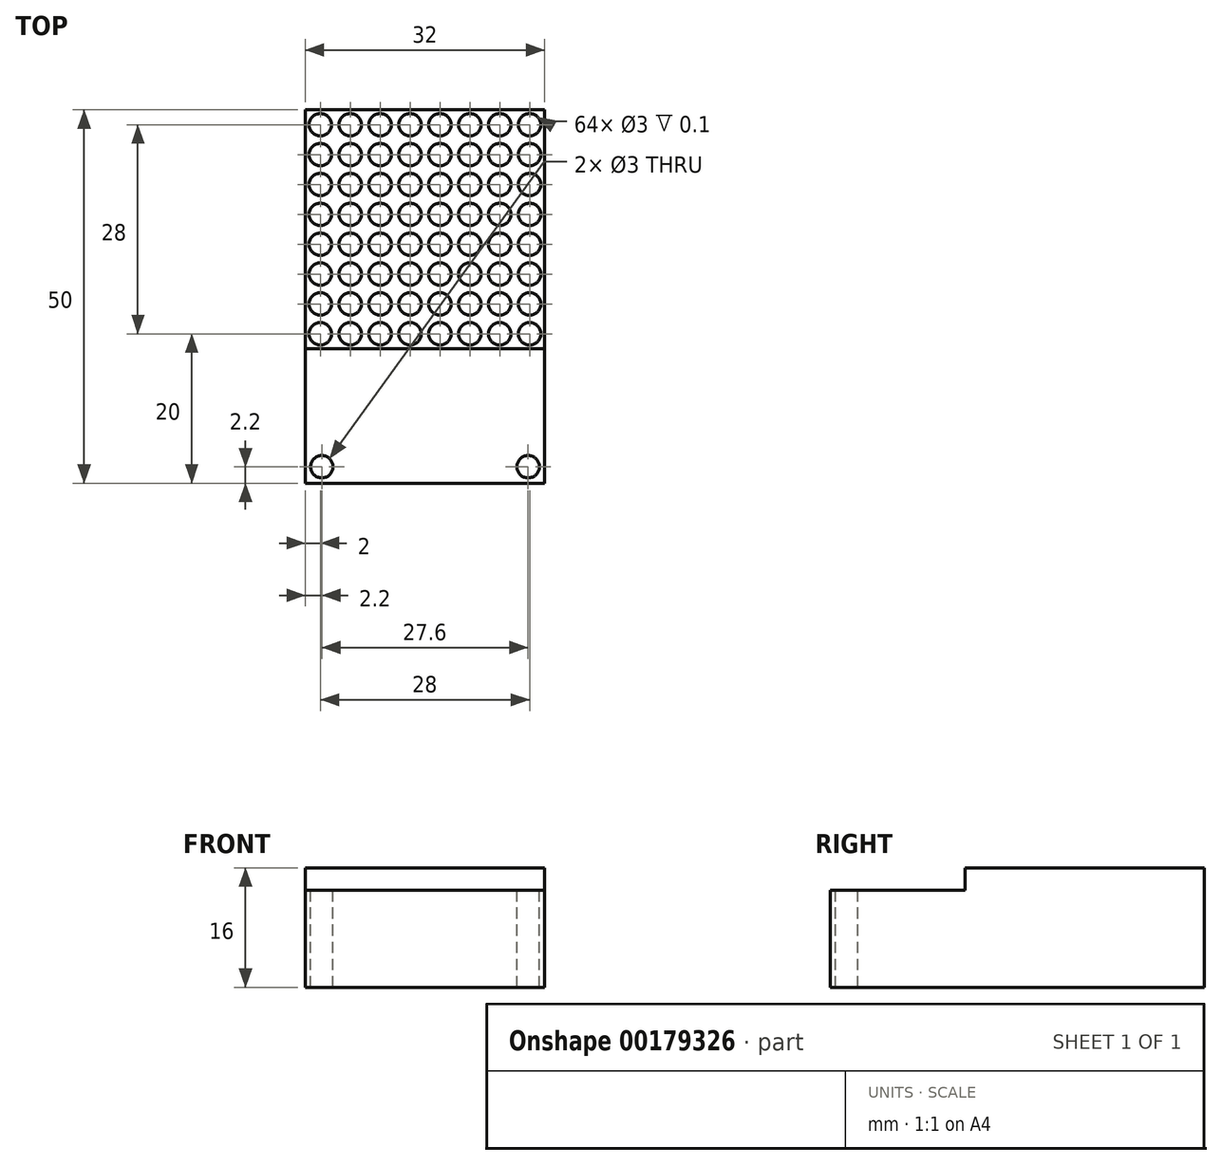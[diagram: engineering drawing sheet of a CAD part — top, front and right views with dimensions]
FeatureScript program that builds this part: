
annotation { "Feature Type Name" : "Feature", "Feature Type Description" : "" }
export const myFeature = defineFeature(function(context is Context, id is Id, definition is map)
    precondition{}
    {
        {
            var Q0;
            Q0=qCreatedBy(makeId("Top.planeOp"),FACE);
            var sketch = newSketch(context, id + "F0", { "sketchPlane" : qUnion([Q0])});
            skLineSegment(sketch, "E0.bottom", {"start": v(16, 16) * mm, "end": v(-16, 16) * mm});
            skLineSegment(sketch, "E0.top", {"start": v(16, -16) * mm, "end": v(-16, -16) * mm});
            skLineSegment(sketch, "E0.left", {"start": v(16, 16) * mm, "end": v(16, -16) * mm});
            skLineSegment(sketch, "E0.right", {"start": v(-16, 16) * mm, "end": v(-16, -16) * mm});
            skPoint(sketch, "E0.middle", {"position": v(0, 0) * mm});
            skSolve(sketch);
        }
        {
            var Q0;
            Q0=makeQuery(id+"F0.imprint","IMPRINT",FACE,{"disambiguationData":[TD([[makeQuery(id+"F0.imprint","IMPRINT",EDGE,{"derivedFrom":sQuery(id+"F0.wireOp",EDGE,"E0.bottom")}),1.0]])]});
            extrude(context, id + "F1", {"entities" : qUnion([Q0]), "depth" : 3 * mm});
        }
        {
            var Q0;
            Q0=makeQuery(id+"F1.opExtrude","CAP_FACE",FACE,{"disambiguationData":[OSD([sQuery(id+"F0.wireOp",EDGE,"E0.bottom"),sQuery(id+"F0.wireOp",EDGE,"E0.top"),sQuery(id+"F0.wireOp",EDGE,"E0.left"),sQuery(id+"F0.wireOp",EDGE,"E0.right")])],"isStart":true});
            var sketch = newSketch(context, id + "F2", { "sketchPlane" : qUnion([Q0])});
            skLineSegment(sketch, "E1.bottom", {"start": v(16, -16) * mm, "end": v(-16, -16) * mm});
            skLineSegment(sketch, "E1.top", {"start": v(16, 34) * mm, "end": v(-16, 34) * mm});
            skLineSegment(sketch, "E1.left", {"start": v(16, -16) * mm, "end": v(16, 34) * mm});
            skLineSegment(sketch, "E1.right", {"start": v(-16, -16) * mm, "end": v(-16, 34) * mm});
            skSolve(sketch);
        }
        {
            var Q0;
            Q0 = qSketchRegion(id + "F2", true);
            extrude(context, id + "F3", {"entities" : qUnion([Q0]), "operationType" : NewBodyOperationType.ADD, "depth" : 13 * mm});
        }
        {
            var Q0;
            Q0=makeQuery(id+"F1.opExtrude","CAP_FACE",FACE,{"disambiguationData":[OSD([sQuery(id+"F0.wireOp",EDGE,"E0.bottom"),sQuery(id+"F0.wireOp",EDGE,"E0.top"),sQuery(id+"F0.wireOp",EDGE,"E0.left"),sQuery(id+"F0.wireOp",EDGE,"E0.right")])],"isStart":false});
            var sketch = newSketch(context, id + "F4", { "sketchPlane" : qUnion([Q0])});
            skCircle(sketch, "E2", {"center": v(14, 14) * mm, "radius": 1.5 * mm});
            skCircle(sketch, "E3.0.1.0", {"center": v(14, 10) * mm, "radius": 1.5 * mm});
            skCircle(sketch, "E3.0.2.0", {"center": v(14, 6) * mm, "radius": 1.5 * mm});
            skCircle(sketch, "E3.0.3.0", {"center": v(14, 2) * mm, "radius": 1.5 * mm});
            skCircle(sketch, "E3.0.4.0", {"center": v(14, -2) * mm, "radius": 1.5 * mm});
            skCircle(sketch, "E3.0.5.0", {"center": v(14, -6) * mm, "radius": 1.5 * mm});
            skCircle(sketch, "E3.0.6.0", {"center": v(14, -10) * mm, "radius": 1.5 * mm});
            skCircle(sketch, "E3.0.7.0", {"center": v(14, -14) * mm, "radius": 1.5 * mm});
            skCircle(sketch, "E3.1.0.0", {"center": v(10, 14) * mm, "radius": 1.5 * mm});
            skCircle(sketch, "E3.1.1.0", {"center": v(10, 10) * mm, "radius": 1.5 * mm});
            skCircle(sketch, "E3.1.2.0", {"center": v(10, 6) * mm, "radius": 1.5 * mm});
            skCircle(sketch, "E3.1.3.0", {"center": v(10, 2) * mm, "radius": 1.5 * mm});
            skCircle(sketch, "E3.1.4.0", {"center": v(10, -2) * mm, "radius": 1.5 * mm});
            skCircle(sketch, "E3.1.5.0", {"center": v(10, -6) * mm, "radius": 1.5 * mm});
            skCircle(sketch, "E3.1.6.0", {"center": v(10, -10) * mm, "radius": 1.5 * mm});
            skCircle(sketch, "E3.1.7.0", {"center": v(10, -14) * mm, "radius": 1.5 * mm});
            skCircle(sketch, "E3.2.0.0", {"center": v(6, 14) * mm, "radius": 1.5 * mm});
            skCircle(sketch, "E3.2.1.0", {"center": v(6, 10) * mm, "radius": 1.5 * mm});
            skCircle(sketch, "E3.2.2.0", {"center": v(6, 6) * mm, "radius": 1.5 * mm});
            skCircle(sketch, "E3.2.3.0", {"center": v(6, 2) * mm, "radius": 1.5 * mm});
            skCircle(sketch, "E3.2.4.0", {"center": v(6, -2) * mm, "radius": 1.5 * mm});
            skCircle(sketch, "E3.2.5.0", {"center": v(6, -6) * mm, "radius": 1.5 * mm});
            skCircle(sketch, "E3.2.6.0", {"center": v(6, -10) * mm, "radius": 1.5 * mm});
            skCircle(sketch, "E3.2.7.0", {"center": v(6, -14) * mm, "radius": 1.5 * mm});
            skCircle(sketch, "E3.3.0.0", {"center": v(2, 14) * mm, "radius": 1.5 * mm});
            skCircle(sketch, "E3.3.1.0", {"center": v(2, 10) * mm, "radius": 1.5 * mm});
            skCircle(sketch, "E3.3.2.0", {"center": v(2, 6) * mm, "radius": 1.5 * mm});
            skCircle(sketch, "E3.3.3.0", {"center": v(2, 2) * mm, "radius": 1.5 * mm});
            skCircle(sketch, "E3.3.4.0", {"center": v(2, -2) * mm, "radius": 1.5 * mm});
            skCircle(sketch, "E3.3.5.0", {"center": v(2, -6) * mm, "radius": 1.5 * mm});
            skCircle(sketch, "E3.3.6.0", {"center": v(2, -10) * mm, "radius": 1.5 * mm});
            skCircle(sketch, "E3.3.7.0", {"center": v(2, -14) * mm, "radius": 1.5 * mm});
            skCircle(sketch, "E3.4.0.0", {"center": v(-2, 14) * mm, "radius": 1.5 * mm});
            skCircle(sketch, "E3.4.1.0", {"center": v(-2, 10) * mm, "radius": 1.5 * mm});
            skCircle(sketch, "E3.4.2.0", {"center": v(-2, 6) * mm, "radius": 1.5 * mm});
            skCircle(sketch, "E3.4.3.0", {"center": v(-2, 2) * mm, "radius": 1.5 * mm});
            skCircle(sketch, "E3.4.4.0", {"center": v(-2, -2) * mm, "radius": 1.5 * mm});
            skCircle(sketch, "E3.4.5.0", {"center": v(-2, -6) * mm, "radius": 1.5 * mm});
            skCircle(sketch, "E3.4.6.0", {"center": v(-2, -10) * mm, "radius": 1.5 * mm});
            skCircle(sketch, "E3.4.7.0", {"center": v(-2, -14) * mm, "radius": 1.5 * mm});
            skCircle(sketch, "E3.5.0.0", {"center": v(-6, 14) * mm, "radius": 1.5 * mm});
            skCircle(sketch, "E3.5.1.0", {"center": v(-6, 10) * mm, "radius": 1.5 * mm});
            skCircle(sketch, "E3.5.2.0", {"center": v(-6, 6) * mm, "radius": 1.5 * mm});
            skCircle(sketch, "E3.5.3.0", {"center": v(-6, 2) * mm, "radius": 1.5 * mm});
            skCircle(sketch, "E3.5.4.0", {"center": v(-6, -2) * mm, "radius": 1.5 * mm});
            skCircle(sketch, "E3.5.5.0", {"center": v(-6, -6) * mm, "radius": 1.5 * mm});
            skCircle(sketch, "E3.5.6.0", {"center": v(-6, -10) * mm, "radius": 1.5 * mm});
            skCircle(sketch, "E3.5.7.0", {"center": v(-6, -14) * mm, "radius": 1.5 * mm});
            skCircle(sketch, "E3.6.0.0", {"center": v(-10, 14) * mm, "radius": 1.5 * mm});
            skCircle(sketch, "E3.6.1.0", {"center": v(-10, 10) * mm, "radius": 1.5 * mm});
            skCircle(sketch, "E3.6.2.0", {"center": v(-10, 6) * mm, "radius": 1.5 * mm});
            skCircle(sketch, "E3.6.3.0", {"center": v(-10, 2) * mm, "radius": 1.5 * mm});
            skCircle(sketch, "E3.6.4.0", {"center": v(-10, -2) * mm, "radius": 1.5 * mm});
            skCircle(sketch, "E3.6.5.0", {"center": v(-10, -6) * mm, "radius": 1.5 * mm});
            skCircle(sketch, "E3.6.6.0", {"center": v(-10, -10) * mm, "radius": 1.5 * mm});
            skCircle(sketch, "E3.6.7.0", {"center": v(-10, -14) * mm, "radius": 1.5 * mm});
            skCircle(sketch, "E3.7.0.0", {"center": v(-14, 14) * mm, "radius": 1.5 * mm});
            skCircle(sketch, "E3.7.1.0", {"center": v(-14, 10) * mm, "radius": 1.5 * mm});
            skCircle(sketch, "E3.7.2.0", {"center": v(-14, 6) * mm, "radius": 1.5 * mm});
            skCircle(sketch, "E3.7.3.0", {"center": v(-14, 2) * mm, "radius": 1.5 * mm});
            skCircle(sketch, "E3.7.4.0", {"center": v(-14, -2) * mm, "radius": 1.5 * mm});
            skCircle(sketch, "E3.7.5.0", {"center": v(-14, -6) * mm, "radius": 1.5 * mm});
            skCircle(sketch, "E3.7.6.0", {"center": v(-14, -10) * mm, "radius": 1.5 * mm});
            skCircle(sketch, "E3.7.7.0", {"center": v(-14, -14) * mm, "radius": 1.5 * mm});
            skLineSegment(sketch, "E3.direction1", {"start": v(14, 14) * mm, "end": v(10, 14) * mm, "construction": true});
            skLineSegment(sketch, "E3.direction2", {"start": v(14, 14) * mm, "end": v(14, 10) * mm, "construction": true});
            skSolve(sketch);
        }
        {
            var Q0;
            Q0 = qSketchRegion(id + "F4", true);
            extrude(context, id + "F5", {"entities" : qUnion([Q0]), "operationType" : NewBodyOperationType.REMOVE, "oppositeDirection" : true, "depth" : 0.1 * mm});
        }
        {
            var Q0;
            Q0=makeQuery(id+"F3.opExtrude","CAP_FACE",FACE,{"disambiguationData":[OSD([sQuery(id+"F2.wireOp",EDGE,"E1.bottom"),sQuery(id+"F2.wireOp",EDGE,"E1.top"),sQuery(id+"F2.wireOp",EDGE,"E1.left"),sQuery(id+"F2.wireOp",EDGE,"E1.right")])],"isStart":true});
            var sketch = newSketch(context, id + "F6", { "sketchPlane" : qUnion([Q0])});
            skCircle(sketch, "E4", {"center": v(-13.8, -31.8) * mm, "radius": 1.5 * mm});
            skCircle(sketch, "E5", {"center": v(13.8, -31.8) * mm, "radius": 1.5 * mm});
            skSolve(sketch);
        }
        {
            var Q0;
            Q0 = qSketchRegion(id + "F6", true);
            extrude(context, id + "F7", {"entities" : qUnion([Q0]), "operationType" : NewBodyOperationType.REMOVE, "endBound" : BoundingType.THROUGH_ALL, "oppositeDirection" : true, "depth" : 25 * mm});
        }
    });
